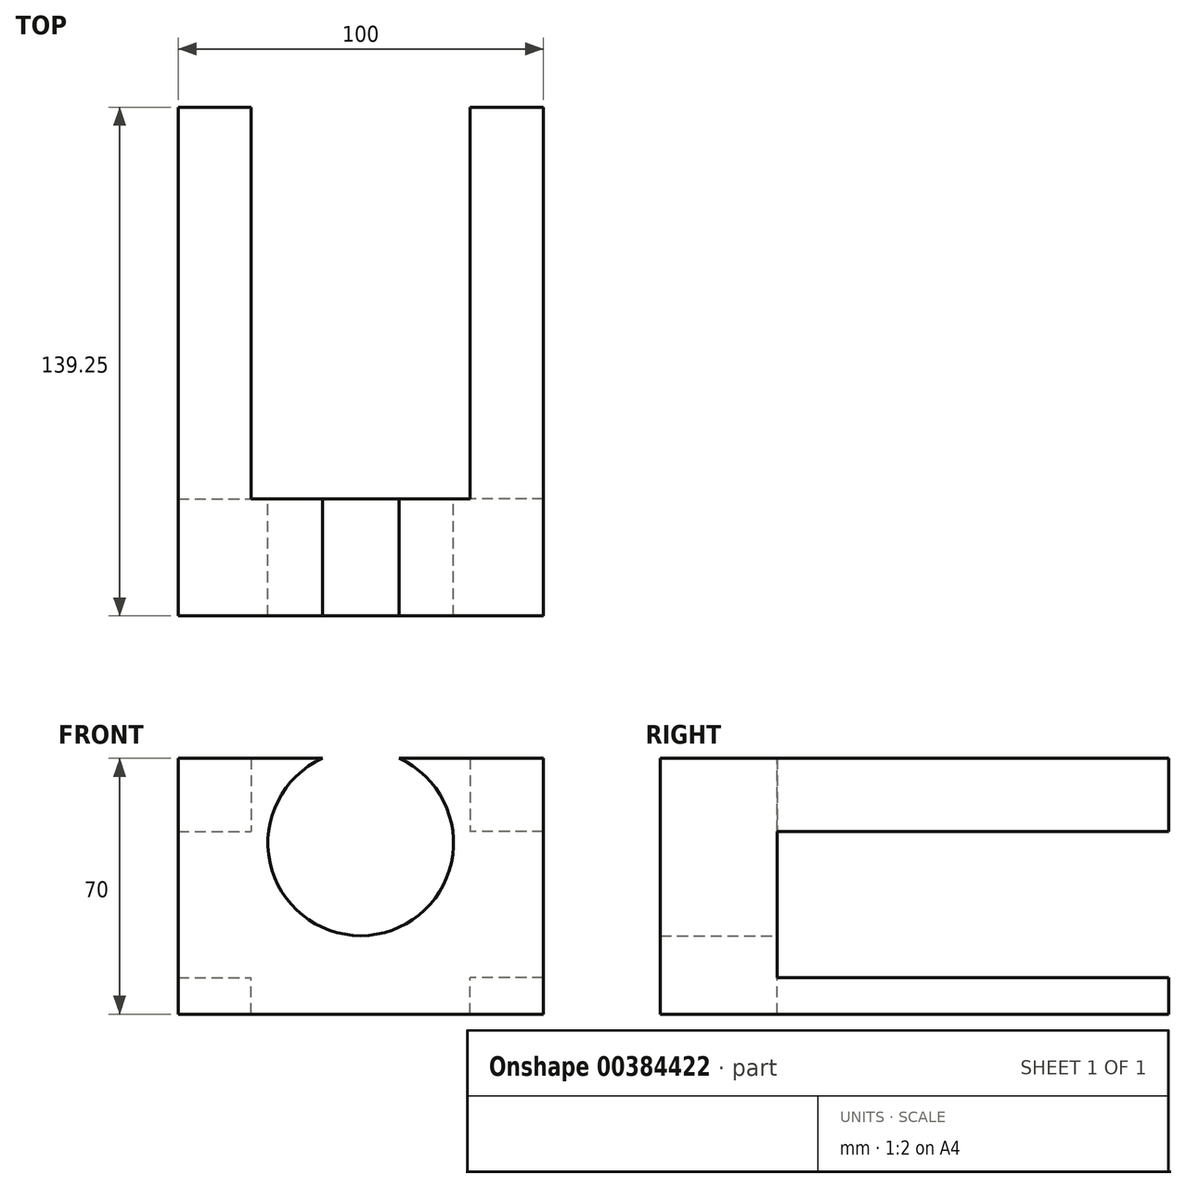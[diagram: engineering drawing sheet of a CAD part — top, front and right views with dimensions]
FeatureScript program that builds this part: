
annotation { "Feature Type Name" : "Feature", "Feature Type Description" : "" }
export const myFeature = defineFeature(function(context is Context, id is Id, definition is map)
    precondition{}
    {
        {
            var Q0;
            Q0=qCreatedBy(makeId("Front.planeOp"),FACE);
            var sketch = newSketch(context, id + "F0", { "sketchPlane" : qUnion([Q0])});
            skLineSegment(sketch, "E0.bottom", {"start": v(50, 40) * mm, "end": v(10.5, 40) * mm});
            skLineSegment(sketch, "E0.top", {"start": v(50, -40) * mm, "end": v(-50, -40) * mm});
            skLineSegment(sketch, "E0.left", {"start": v(50, 40) * mm, "end": v(50, -40) * mm});
            skLineSegment(sketch, "E0.right", {"start": v(-50, 40) * mm, "end": v(-50, -40) * mm});
            skPoint(sketch, "E0.middle", {"position": v(0, 0) * mm});
            skArc(sketch, "E1", {"start": v(-10.5, 40) * mm, "mid": v(0, -8.52) * mm, "end": v(10.5, 40) * mm});
            skLineSegment(sketch, "E2.trimOffspring", {"start": v(-10.5, 40) * mm, "end": v(-50, 40) * mm});
            skSolve(sketch);
        }
        {
            var Q0;
            Q0=makeQuery(id+"F0.imprint","IMPRINT",FACE,{"disambiguationData":[TD([[makeQuery(id+"F0.imprint","IMPRINT",EDGE,{"derivedFrom":sQuery(id+"F0.wireOp",EDGE,"E0.bottom")}),1.0]])]});
            extrude(context, id + "F1", {"entities" : qUnion([Q0]), "depth" : 32 * mm});
        }
        {
            var Q0;
            Q0=makeQuery(id+"F1.opExtrude","CAP_FACE",FACE,{"disambiguationData":[OSD([sQuery(id+"F0.wireOp",EDGE,"E0.bottom"),sQuery(id+"F0.wireOp",EDGE,"E0.top"),sQuery(id+"F0.wireOp",EDGE,"E0.left"),sQuery(id+"F0.wireOp",EDGE,"E0.right"),sQuery(id+"F0.wireOp",EDGE,"E1"),sQuery(id+"F0.wireOp",EDGE,"E2.trimOffspring")])],"isStart":true});
            var sketch = newSketch(context, id + "F2", { "sketchPlane" : qUnion([Q0])});
            skLineSegment(sketch, "E3.bottom", {"start": v(-50, 40) * mm, "end": v(-30, 40) * mm});
            skLineSegment(sketch, "E3.top", {"start": v(-50, 20) * mm, "end": v(-30, 20) * mm});
            skLineSegment(sketch, "E3.left", {"start": v(-50, 40) * mm, "end": v(-50, 20) * mm});
            skLineSegment(sketch, "E3.right", {"start": v(-30, 40) * mm, "end": v(-30, 20) * mm});
            skLineSegment(sketch, "E4.bottom", {"start": v(-50, -40) * mm, "end": v(-30, -40) * mm});
            skLineSegment(sketch, "E4.top", {"start": v(-50, -20) * mm, "end": v(-30, -20) * mm});
            skLineSegment(sketch, "E4.left", {"start": v(-50, -40) * mm, "end": v(-50, -20) * mm});
            skLineSegment(sketch, "E4.right", {"start": v(-30, -40) * mm, "end": v(-30, -20) * mm});
            skLineSegment(sketch, "E5.bottom", {"start": v(50, 40) * mm, "end": v(30, 40) * mm});
            skLineSegment(sketch, "E5.top", {"start": v(50, 20) * mm, "end": v(30, 20) * mm});
            skLineSegment(sketch, "E5.left", {"start": v(50, 40) * mm, "end": v(50, 20) * mm});
            skLineSegment(sketch, "E5.right", {"start": v(30, 40) * mm, "end": v(30, 20) * mm});
            skLineSegment(sketch, "E6.bottom", {"start": v(50, -40) * mm, "end": v(30, -40) * mm});
            skLineSegment(sketch, "E6.top", {"start": v(50, -20) * mm, "end": v(30, -20) * mm});
            skLineSegment(sketch, "E6.left", {"start": v(50, -40) * mm, "end": v(50, -20) * mm});
            skLineSegment(sketch, "E6.right", {"start": v(30, -40) * mm, "end": v(30, -20) * mm});
            skSolve(sketch);
        }
        {
            var Q0;
            Q0=makeQuery(id+"F2.imprint","IMPRINT",FACE,{"disambiguationData":[TD([[makeQuery(id+"F2.imprint","IMPRINT",EDGE,{"derivedFrom":sQuery(id+"F2.wireOp",EDGE,"E3.bottom")}),-1.0]])]});
            var Q1;
            Q1=makeQuery(id+"F2.imprint","IMPRINT",FACE,{"disambiguationData":[TD([[makeQuery(id+"F2.imprint","IMPRINT",EDGE,{"derivedFrom":sQuery(id+"F2.wireOp",EDGE,"E5.bottom")}),-1.0]])]});
            var Q2;
            Q2=makeQuery(id+"F2.imprint","IMPRINT",FACE,{"disambiguationData":[TD([[makeQuery(id+"F2.imprint","IMPRINT",EDGE,{"derivedFrom":sQuery(id+"F2.wireOp",EDGE,"E6.bottom")}),1.0]])]});
            var Q3;
            Q3=makeQuery(id+"F2.imprint","IMPRINT",FACE,{"disambiguationData":[TD([[makeQuery(id+"F2.imprint","IMPRINT",EDGE,{"derivedFrom":sQuery(id+"F2.wireOp",EDGE,"E4.bottom")}),1.0]])]});
            extrude(context, id + "F3", {"entities" : qUnion([Q0, Q1, Q2, Q3]), "operationType" : NewBodyOperationType.ADD, "depth" : 107.25 * mm});
        }
        {
            var Q0;
            Q0=makeQuery(id+"F3.boolean.opBoolean","MERGE",FACE,{"derivedFrom":[makeQuery(id+"F1.opExtrude","SWEPT_FACE",FACE,{"disambiguationData":[OSD([sQuery(id+"F0.wireOp",EDGE,"E0.left")])]}),makeQuery(id+"F3.opExtrude","SWEPT_FACE",FACE,{"disambiguationData":[OSD([sQuery(id+"F2.wireOp",EDGE,"E3.left")])]}),makeQuery(id+"F3.opExtrude","SWEPT_FACE",FACE,{"disambiguationData":[OSD([sQuery(id+"F2.wireOp",EDGE,"E4.left")])]})]});
            var sketch = newSketch(context, id + "F4", { "sketchPlane" : qUnion([Q0])});
            skLineSegment(sketch, "E7", {"start": v(107.25, -30) * mm, "end": v(107.25, -40) * mm});
            skLineSegment(sketch, "E8", {"start": v(-32, -40) * mm, "end": v(-32, -30) * mm});
            skLineSegment(sketch, "E9", {"start": v(-32, -30) * mm, "end": v(107.25, -30) * mm});
            skLineSegment(sketch, "E10", {"start": v(-32, -40) * mm, "end": v(107.25, -40) * mm});
            skPoint(sketch, "E11.orphan", {"position": v(-32, -20) * mm});
            skSolve(sketch);
        }
        {
            var Q0;
            Q0=makeQuery(id+"F4.imprint","IMPRINT",FACE,{"disambiguationData":[TD([[makeQuery(id+"F4.imprint","IMPRINT",EDGE,{"derivedFrom":sQuery(id+"F4.wireOp",EDGE,"E7")}),-1.0]])]});
            extrude(context, id + "F5", {"entities" : qUnion([Q0]), "operationType" : NewBodyOperationType.REMOVE, "oppositeDirection" : true, "depth" : 150 * mm});
        }
    });
